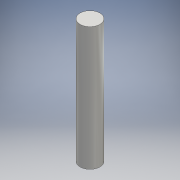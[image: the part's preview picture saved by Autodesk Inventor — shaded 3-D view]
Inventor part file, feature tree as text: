
AUTODESK INVENTOR PART (.ipt)
format: ipt  version: 2020.2 (Build 242310000, 310)  size: 87,552 bytes
history: native  units: mm
features: other x1, extrude x1, sketch x1
ambient origin geometry x8: Origin, YZ Plane, XZ Plane, XY Plane, X Axis, Y Axis, Z Axis, Center Point
bodies: Body1 (feature_tree)
feature tree (3):
  other  "ソリッド1"
  extrude  "押し出し1"  Depth=4.0mm
  sketch  "スケッチ1"
